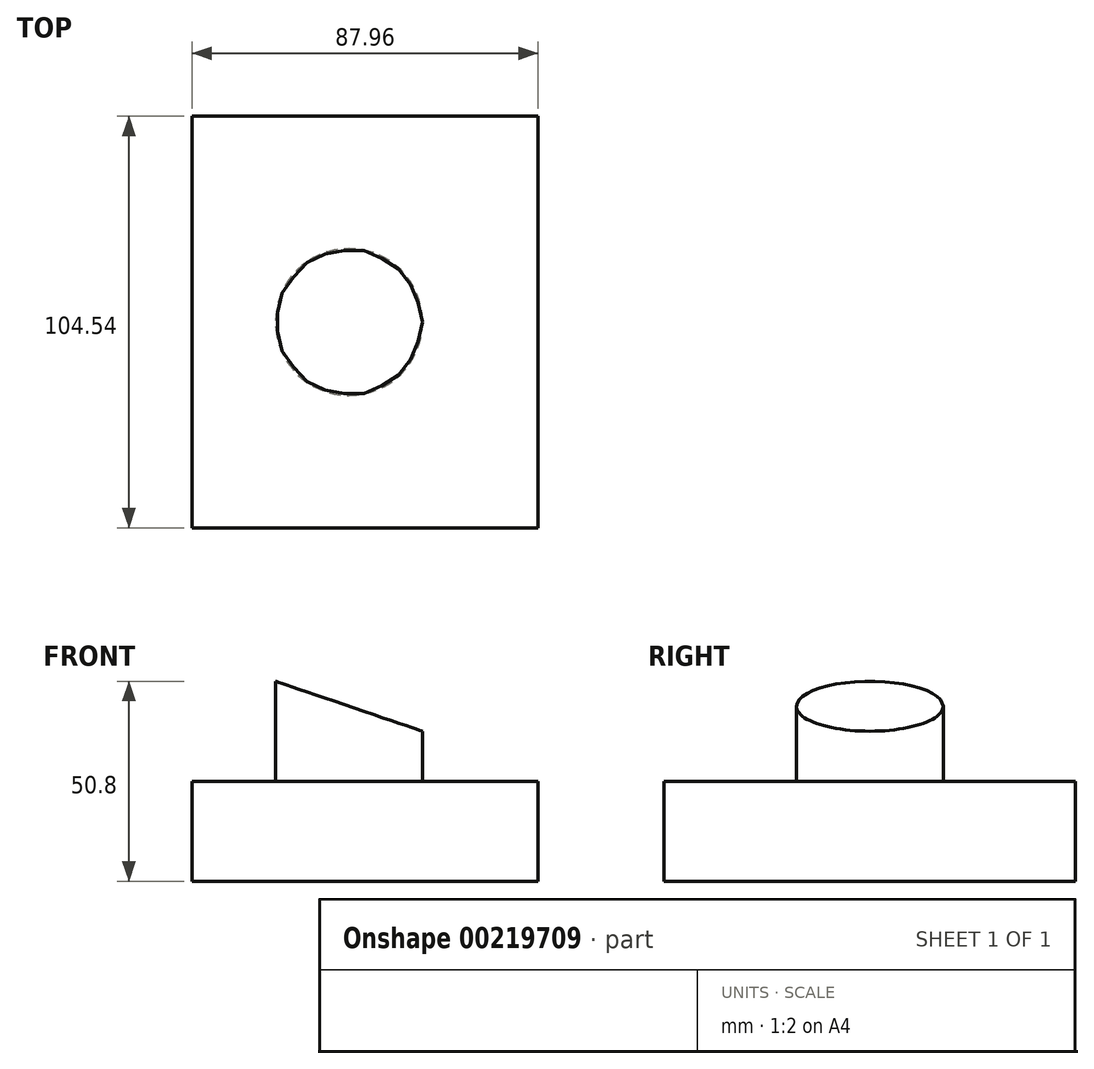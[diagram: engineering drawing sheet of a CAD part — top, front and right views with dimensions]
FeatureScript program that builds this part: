
annotation { "Feature Type Name" : "Feature", "Feature Type Description" : "" }
export const myFeature = defineFeature(function(context is Context, id is Id, definition is map)
    precondition{}
    {
        {
            var Q0;
            Q0=qCreatedBy(makeId("Top.planeOp"),FACE);
            var sketch = newSketch(context, id + "F0", { "sketchPlane" : qUnion([Q0])});
            skLineSegment(sketch, "E0.bottom", {"start": v(43.98, -52.27) * mm, "end": v(-43.98, -52.27) * mm});
            skLineSegment(sketch, "E0.top", {"start": v(43.98, 52.27) * mm, "end": v(-43.98, 52.27) * mm});
            skLineSegment(sketch, "E0.left", {"start": v(43.98, -52.27) * mm, "end": v(43.98, 52.27) * mm});
            skLineSegment(sketch, "E0.right", {"start": v(-43.98, -52.27) * mm, "end": v(-43.98, 52.27) * mm});
            skPoint(sketch, "E0.middle", {"position": v(0, 0) * mm});
            skSolve(sketch);
        }
        {
            var Q0;
            Q0=makeQuery(id+"F0.imprint","IMPRINT",FACE,{"disambiguationData":[TD([[makeQuery(id+"F0.imprint","IMPRINT",EDGE,{"derivedFrom":sQuery(id+"F0.wireOp",EDGE,"E0.bottom")}),-1.0]])]});
            extrude(context, id + "F1", {"entities" : qUnion([Q0]), "depth" : 25.4 * mm});
        }
        {
            var Q0;
            Q0=makeQuery(id+"F1.opExtrude","CAP_FACE",FACE,{"disambiguationData":[OSD([sQuery(id+"F0.wireOp",EDGE,"E0.bottom"),sQuery(id+"F0.wireOp",EDGE,"E0.top"),sQuery(id+"F0.wireOp",EDGE,"E0.left"),sQuery(id+"F0.wireOp",EDGE,"E0.right")])],"isStart":false});
            var sketch = newSketch(context, id + "F2", { "sketchPlane" : qUnion([Q0])});
            skCircle(sketch, "E1", {"center": v(-4.06, 0) * mm, "radius": 18.66 * mm});
            skSolve(sketch);
        }
        {
            var Q0;
            Q0=makeQuery(id+"F2.imprint","IMPRINT",FACE,{"disambiguationData":[TD([[makeQuery(id+"F2.imprint","IMPRINT",EDGE,{"derivedFrom":sQuery(id+"F2.wireOp",EDGE,"E1")}),1.0]])]});
            extrude(context, id + "F3", {"entities" : qUnion([Q0]), "operationType" : NewBodyOperationType.ADD, "depth" : 25.4 * mm});
        }
        {
            var Q0;
            Q0=makeQuery(id+"F1.opExtrude","SWEPT_FACE",FACE,{"disambiguationData":[OSD([sQuery(id+"F0.wireOp",EDGE,"E0.bottom")])]});
            var sketch = newSketch(context, id + "F4", { "sketchPlane" : qUnion([Q0])});
            skLineSegment(sketch, "E2.0", {"start": v(-22.72, 50.8) * mm, "end": v(14.6, 50.8) * mm});
            skLineSegment(sketch, "E3", {"start": v(14.6, 50.8) * mm, "end": v(14.6, 25.4) * mm});
            skLineSegment(sketch, "E4", {"start": v(-22.72, 50.8) * mm, "end": v(14.6, 38.1) * mm});
            skSolve(sketch);
        }
        {
            var Q0;
            {var subQ0=sQuery(id+"F4.wireOp",EDGE,"E2.0");Q0=makeQuery(id+"F4.imprint","IMPRINT",FACE,{"disambiguationData":[TD([[makeQuery(id+"F4.imprint","IMPRINT",EDGE,{"derivedFrom":subQ0}),-1.0]])]});}
            extrude(context, id + "F5", {"entities" : qUnion([Q0]), "operationType" : NewBodyOperationType.REMOVE, "endBound" : BoundingType.THROUGH_ALL, "oppositeDirection" : true, "depth" : 25.4 * mm});
        }
    });
